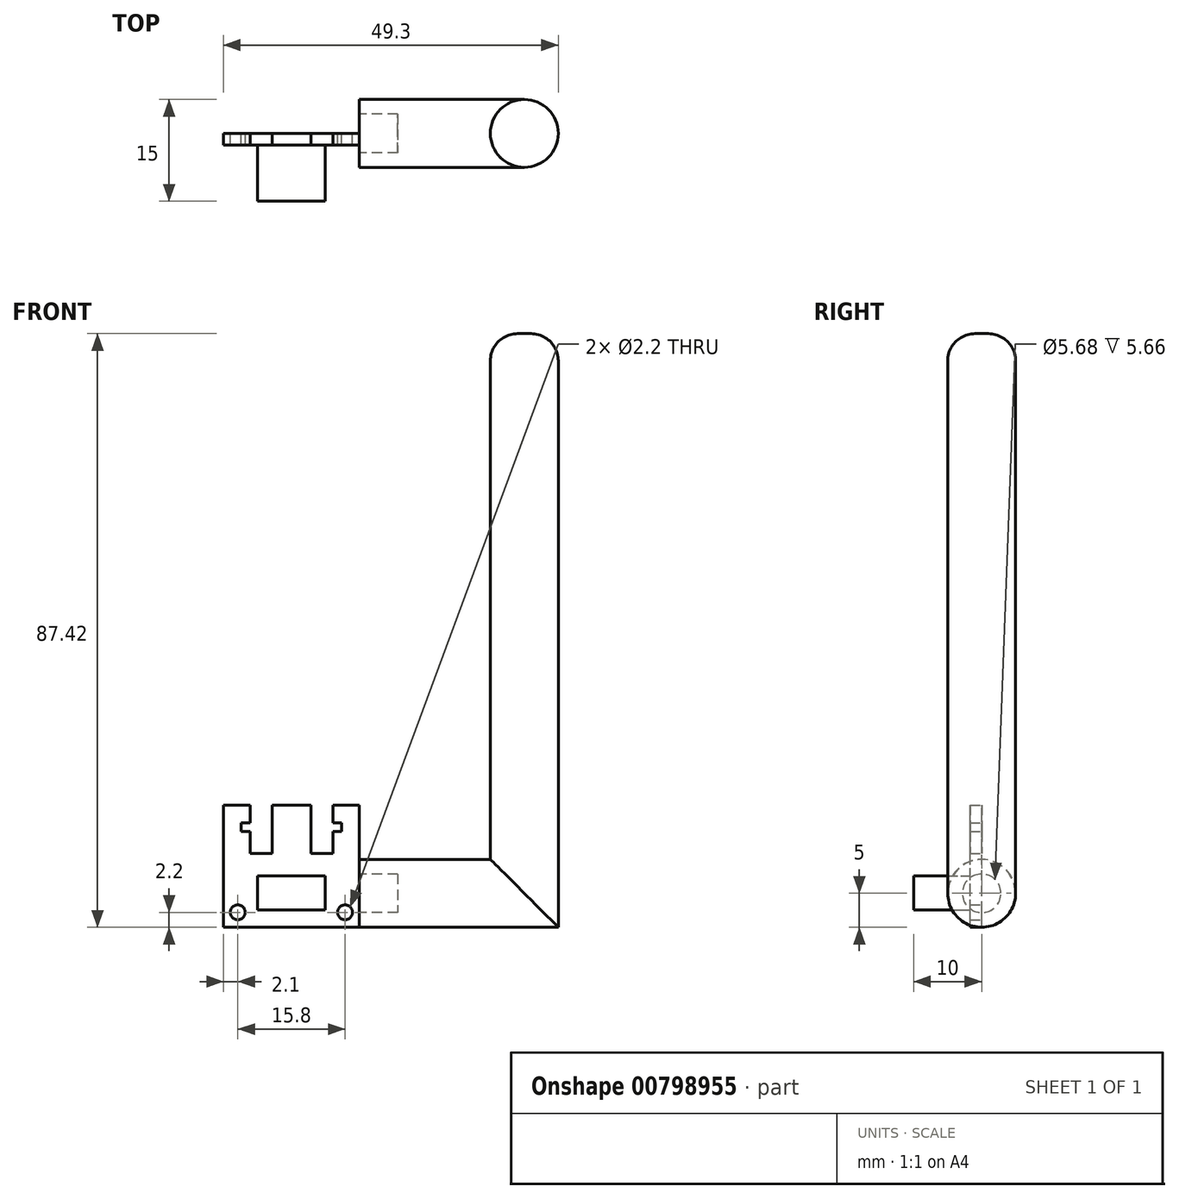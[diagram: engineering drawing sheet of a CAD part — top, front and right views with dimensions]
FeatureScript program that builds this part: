
annotation { "Feature Type Name" : "Feature", "Feature Type Description" : "" }
export const myFeature = defineFeature(function(context is Context, id is Id, definition is map)
    precondition{}
    {
        {
            var Q0;
            Q0=qCreatedBy(makeId("Front.planeOp"),FACE);
            var sketch = newSketch(context, id + "F0", { "sketchPlane" : qUnion([Q0])});
            skLineSegment(sketch, "E0", {"start": v(0, 0) * mm, "end": v(29.3, 0) * mm});
            skLineSegment(sketch, "E1", {"start": v(29.3, 0) * mm, "end": v(29.3, 87.42) * mm});
            skSolve(sketch);
        }
        {
            var Q0;
            Q0=qCreatedBy(makeId("Right.planeOp"),FACE);
            var sketch = newSketch(context, id + "F1", { "sketchPlane" : qUnion([Q0])});
            skCircle(sketch, "E2", {"center": v(0, 5) * mm, "radius": 5 * mm});
            skPoint(sketch, "E2.first.point", {"position": v(0, 0) * mm});
            skPoint(sketch, "E2.second.point", {"position": v(0, 10) * mm});
            skPoint(sketch, "E2.third.point", {"position": v(-4.48, 7.22) * mm});
            skSolve(sketch);
        }
        {
            var Q0;
            Q0=makeQuery(id+"F1.imprint","IMPRINT",FACE,{"disambiguationData":[TD([[makeQuery(id+"F1.imprint","IMPRINT",EDGE,{"derivedFrom":sQuery(id+"F1.wireOp",EDGE,"E2")}),1.0]])]});
            var Q1;
            Q1=sQuery(id+"F0.wireOp",EDGE,"E0");
            var Q2;
            Q2=sQuery(id+"F0.wireOp",EDGE,"E1");
            sweep(context, id + "F2", {"profiles" : qUnion([Q0]), "path" : qUnion([Q1, Q2])});
        }
        {
            var Q0;
            Q0=makeQuery(id+"F2.opSweep","CAP_FACE",FACE,{"disambiguationData":[OSD([sQuery(id+"F0.wireOp",VERTEX,"E1.end"),sQuery(id+"F1.wireOp",EDGE,"E2")])],"isStart":false});
            fillet(context, id + "F3", {"entities" : qUnion([Q0]), "radius" : 4 * mm, "tangentPropagation" : true, "allowEdgeOverflow" : false});
        }
        {
            var Q0;
            Q0=makeQuery(id+"F2.opSweep","CAP_FACE",FACE,{"disambiguationData":[OSD([sQuery(id+"F0.wireOp",VERTEX,"E0.start"),sQuery(id+"F1.wireOp",EDGE,"E2")])],"isStart":true});
            var sketch = newSketch(context, id + "F4", { "sketchPlane" : qUnion([Q0])});
            skCircle(sketch, "E3.0", {"center": v(0, 5) * mm, "radius": 5 * mm, "construction": true});
            skCircle(sketch, "E4", {"center": v(0, 5) * mm, "radius": 2.84 * mm});
            skSolve(sketch);
        }
        {
            var Q0;
            Q0=makeQuery(id+"F4.imprint","IMPRINT",FACE,{"disambiguationData":[TD([[makeQuery(id+"F4.imprint","IMPRINT",EDGE,{"derivedFrom":sQuery(id+"F4.wireOp",EDGE,"E4")}),1.0]])]});
            extrude(context, id + "F5", {"entities" : qUnion([Q0]), "operationType" : NewBodyOperationType.REMOVE, "oppositeDirection" : true, "depth" : 5.66 * mm, "offsetDistance" : 25 * mm});
        }
        {
            var Q0;
            Q0=qCreatedBy(makeId("Front.planeOp"),FACE);
            var sketch = newSketch(context, id + "F6", { "sketchPlane" : qUnion([Q0])});
            skLineSegment(sketch, "E5.bottom", {"start": v(-20, 0) * mm, "end": v(0, 0) * mm});
            skLineSegment(sketch, "E5.top", {"start": v(-20, 18) * mm, "end": v(0, 18) * mm});
            skLineSegment(sketch, "E5.left", {"start": v(-20, 0) * mm, "end": v(-20, 18) * mm});
            skLineSegment(sketch, "E5.right", {"start": v(0, 0) * mm, "end": v(0, 18) * mm});
            skLineSegment(sketch, "E6.left", {"start": v(-16.1, 18) * mm, "end": v(-16.1, 10.89) * mm});
            skLineSegment(sketch, "E6.right", {"start": v(-3.9, 18) * mm, "end": v(-3.9, 10.89) * mm});
            skLineSegment(sketch, "E7.top", {"start": v(-12.85, 18) * mm, "end": v(-7.15, 18) * mm});
            skLineSegment(sketch, "E7.left", {"start": v(-12.85, 10.89) * mm, "end": v(-12.85, 18) * mm});
            skLineSegment(sketch, "E7.right", {"start": v(-7.15, 10.9) * mm, "end": v(-7.15, 18) * mm});
            skCircle(sketch, "E8", {"center": v(-17.9, 2.2) * mm, "radius": 1.1 * mm});
            skLineSegment(sketch, "E9", {"start": v(-20, 1.1) * mm, "end": v(0, 1.1) * mm, "construction": true});
            skLineSegment(sketch, "E10", {"start": v(-19, 18) * mm, "end": v(-19, 0) * mm, "construction": true});
            skLineSegment(sketch, "E11", {"start": v(-1, 18) * mm, "end": v(-1, 0) * mm, "construction": true});
            skCircle(sketch, "E12.1.0.0", {"center": v(-2.1, 2.2) * mm, "radius": 1.1 * mm});
            skLineSegment(sketch, "E12.direction1", {"start": v(-17.9, 2.2) * mm, "end": v(-2.1, 2.2) * mm, "construction": true});
            skLineSegment(sketch, "E13", {"start": v(-16.1, 10.89) * mm, "end": v(-12.85, 10.89) * mm});
            skLineSegment(sketch, "E14", {"start": v(-7.15, 10.9) * mm, "end": v(-3.9, 10.89) * mm});
            skLineSegment(sketch, "E15", {"start": v(-20, 2.55) * mm, "end": v(0, 2.55) * mm, "construction": true});
            skLineSegment(sketch, "E16.bottom", {"start": v(-15, 2.55) * mm, "end": v(-5, 2.55) * mm});
            skLineSegment(sketch, "E16.top", {"start": v(-15, 7.55) * mm, "end": v(-5, 7.55) * mm});
            skLineSegment(sketch, "E16.left", {"start": v(-15, 2.55) * mm, "end": v(-15, 7.55) * mm});
            skLineSegment(sketch, "E16.right", {"start": v(-5, 2.55) * mm, "end": v(-5, 7.55) * mm});
            skLineSegment(sketch, "E17", {"start": v(-16.1, 15.4) * mm, "end": v(-17.4, 15.4) * mm});
            skLineSegment(sketch, "E18", {"start": v(-17.4, 15.4) * mm, "end": v(-17.4, 14.1) * mm});
            skLineSegment(sketch, "E19", {"start": v(-17.4, 14.1) * mm, "end": v(-16.1, 14.1) * mm});
            skLineSegment(sketch, "E20", {"start": v(-3.9, 15.4) * mm, "end": v(-2.6, 15.4) * mm});
            skLineSegment(sketch, "E21", {"start": v(-2.6, 15.4) * mm, "end": v(-2.6, 14.1) * mm});
            skLineSegment(sketch, "E22", {"start": v(-2.6, 14.1) * mm, "end": v(-3.9, 14.1) * mm});
            skSolve(sketch);
        }
        {
            var Q0;
            Q0=makeQuery(id+"F6.imprint","IMPRINT",FACE,{"disambiguationData":[TD([[makeQuery(id+"F6.imprint","IMPRINT",EDGE,{"derivedFrom":sQuery(id+"F6.wireOp",EDGE,"E5.bottom")}),1.0]])]});
            extrude(context, id + "F7", {"entities" : qUnion([Q0]), "depth" : 1.7 * mm, "offsetDistance" : 25 * mm});
        }
        {
            var Q0;
            Q0=makeQuery(id+"F6.imprint","IMPRINT",FACE,{"disambiguationData":[TD([[makeQuery(id+"F6.imprint","IMPRINT",EDGE,{"derivedFrom":sQuery(id+"F6.wireOp",EDGE,"E16.bottom")}),1.0]])]});
            extrude(context, id + "F8", {"entities" : qUnion([Q0]), "operationType" : NewBodyOperationType.ADD, "depth" : 10 * mm, "offsetDistance" : 25 * mm});
        }
    });
